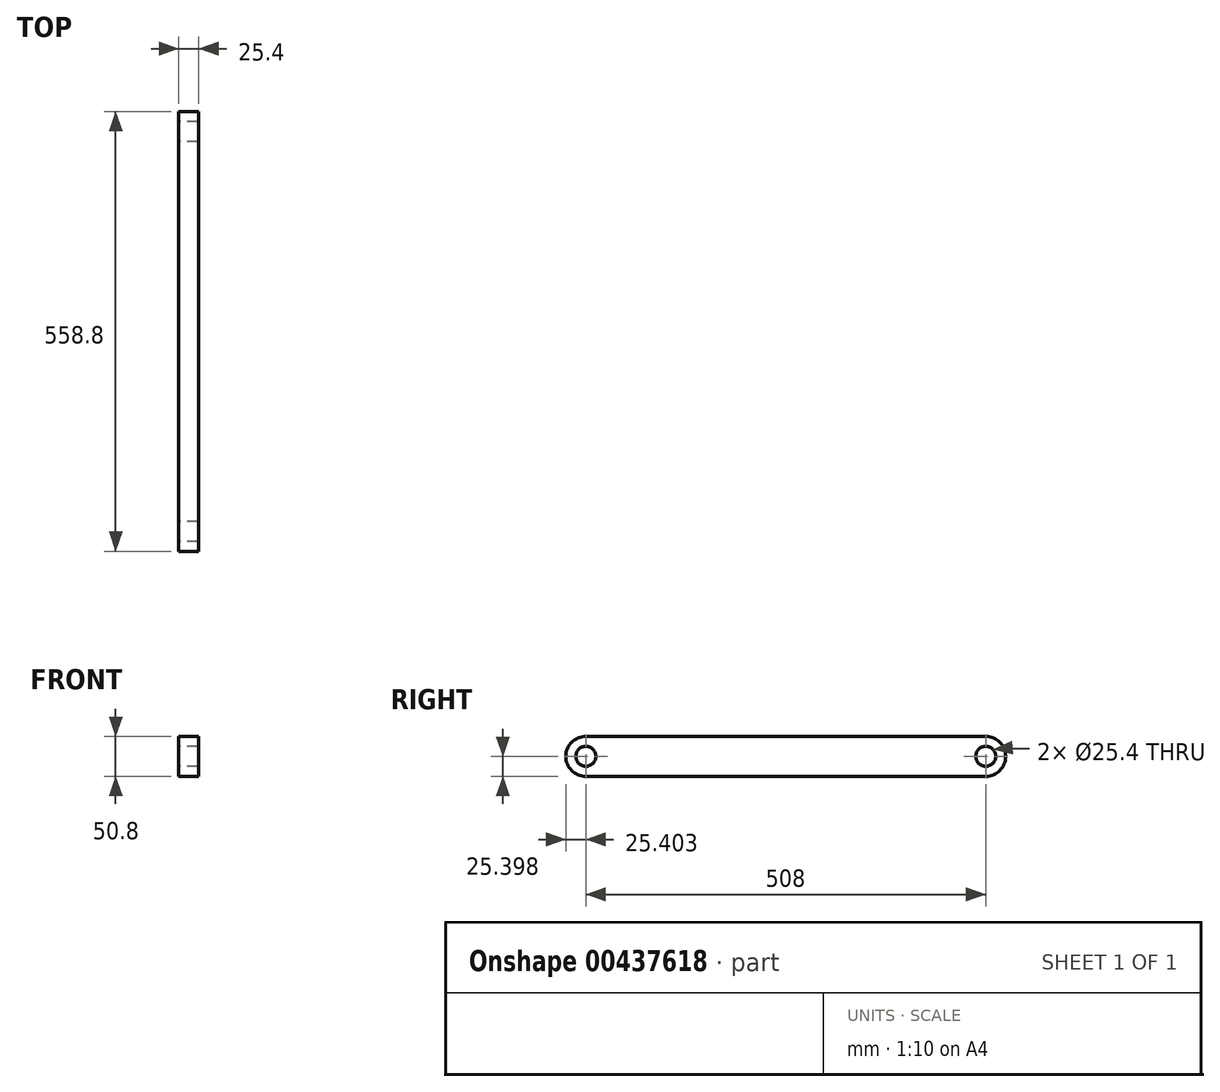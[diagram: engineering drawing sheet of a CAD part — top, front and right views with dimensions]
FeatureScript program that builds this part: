
annotation { "Feature Type Name" : "Feature", "Feature Type Description" : "" }
export const myFeature = defineFeature(function(context is Context, id is Id, definition is map)
    precondition{}
    {
        {
            var Q0;
            Q0=qCreatedBy(makeId("Right.planeOp"),FACE);
            var sketch = newSketch(context, id + "F0", { "sketchPlane" : qUnion([Q0])});
            skLineSegment(sketch, "E0.bottom", {"start": v(-116.88, 13.44) * mm, "end": v(391.12, 13.44) * mm});
            skLineSegment(sketch, "E0.top", {"start": v(-116.88, -37.36) * mm, "end": v(391.12, -37.36) * mm});
            skLineSegment(sketch, "E0.left", {"start": v(-116.88, 13.44) * mm, "end": v(-116.88, -37.36) * mm});
            skLineSegment(sketch, "E0.right", {"start": v(391.12, 13.44) * mm, "end": v(391.12, -37.36) * mm});
            skCircle(sketch, "E1", {"center": v(-116.88, -11.96) * mm, "radius": 25.4 * mm});
            skCircle(sketch, "E2", {"center": v(391.12, -11.96) * mm, "radius": 25.4 * mm});
            skCircle(sketch, "E3", {"center": v(391.12, -11.96) * mm, "radius": 12.7 * mm});
            skCircle(sketch, "E4", {"center": v(-116.88, -11.96) * mm, "radius": 12.7 * mm});
            skSolve(sketch);
        }
        {
            var Q0;
            Q0 = qSketchRegion(id + "F0", true);
            extrude(context, id + "F1", {"entities" : qUnion([Q0]), "depth" : 25.4 * mm});
        }
    });
